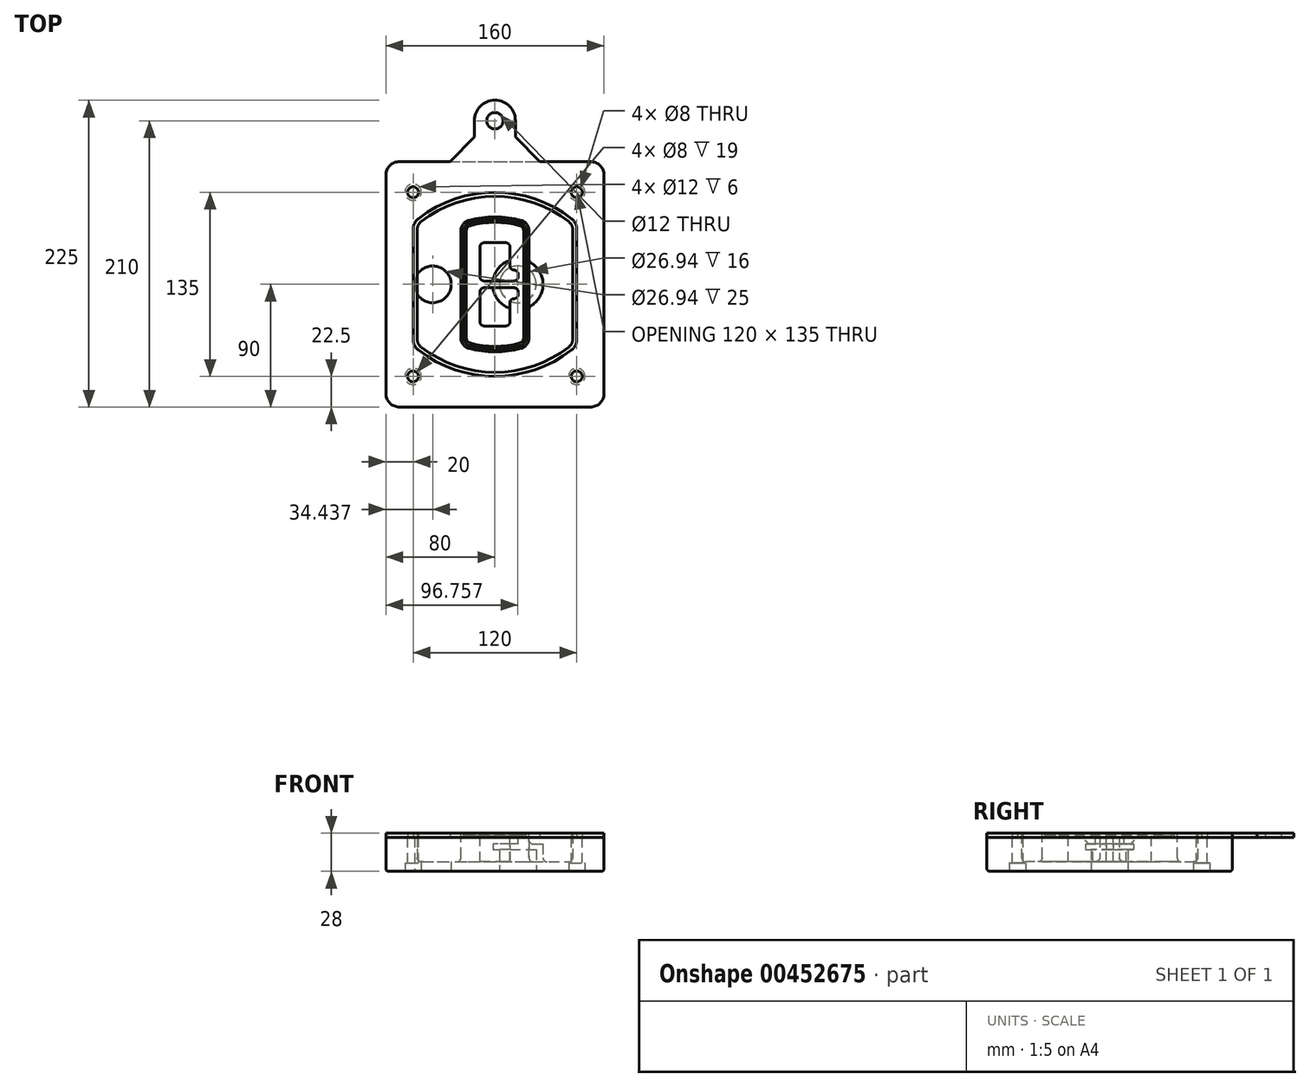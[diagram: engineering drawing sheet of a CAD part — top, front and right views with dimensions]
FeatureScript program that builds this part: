
annotation { "Feature Type Name" : "Feature", "Feature Type Description" : "" }
export const myFeature = defineFeature(function(context is Context, id is Id, definition is map)
    precondition{}
    {
        {
            var Q0;
            Q0=qCreatedBy(makeId("Top.planeOp"),FACE);
            var sketch = newSketch(context, id + "F0", { "sketchPlane" : qUnion([Q0])});
            skPoint(sketch, "E0.rect.middle", {"position": v(0, 0) * mm});
            skLineSegment(sketch, "E1.bottom", {"start": v(-70, -90) * mm, "end": v(70, -90) * mm});
            skLineSegment(sketch, "E1.top", {"start": v(-70, 90) * mm, "end": v(70, 90) * mm});
            skLineSegment(sketch, "E1.left", {"start": v(-80, -80) * mm, "end": v(-80, 80) * mm});
            skLineSegment(sketch, "E1.right", {"start": v(80, -80) * mm, "end": v(80, 80) * mm});
            skLineSegment(sketch, "E2", {"start": v(-80, 90) * mm, "end": v(80, -90) * mm, "construction": true});
            skLineSegment(sketch, "E3", {"start": v(80, 90) * mm, "end": v(-80, -90) * mm, "construction": true});
            skCircle(sketch, "E4", {"center": v(-60, 67.5) * mm, "radius": 4 * mm});
            skCircle(sketch, "E5", {"center": v(60, 67.5) * mm, "radius": 4 * mm});
            skCircle(sketch, "E6", {"center": v(60, -67.5) * mm, "radius": 4 * mm});
            skCircle(sketch, "E7", {"center": v(-60, -67.5) * mm, "radius": 4 * mm});
            skLineSegment(sketch, "E8", {"start": v(-60, 67.5) * mm, "end": v(60, 67.5) * mm, "construction": true});
            skLineSegment(sketch, "E9", {"start": v(60, 67.5) * mm, "end": v(60, -67.5) * mm, "construction": true});
            skLineSegment(sketch, "E10", {"start": v(60, -67.5) * mm, "end": v(-60, -67.5) * mm, "construction": true});
            skLineSegment(sketch, "E11", {"start": v(-60, -67.5) * mm, "end": v(-60, 67.5) * mm, "construction": true});
            skLineSegment(sketch, "E12", {"start": v(-60, 40.3) * mm, "end": v(-60, -40.3) * mm});
            skLineSegment(sketch, "E13", {"start": v(60, 40.3) * mm, "end": v(60, -40.3) * mm});
            skArc(sketch, "E14", {"start": v(56.15, 48.18) * mm, "mid": v(0, 67.5) * mm, "end": v(-56.15, 48.18) * mm});
            skArc(sketch, "E15", {"start": v(-56.15, -48.18) * mm, "mid": v(0, -67.5) * mm, "end": v(56.15, -48.18) * mm});
            skLineSegment(sketch, "E16", {"start": v(-60, 0) * mm, "end": v(60, 0) * mm, "construction": true});
            skPoint(sketch, "E17.visualSharp", {"position": v(-60, -45) * mm});
            skArc(sketch, "E17.filletArc", {"start": v(-60, -40.3) * mm, "mid": v(-58.99, -44.68) * mm, "end": v(-56.15, -48.18) * mm});
            skPoint(sketch, "E18.visualSharp", {"position": v(-60, 45) * mm});
            skArc(sketch, "E18.filletArc", {"start": v(-56.15, 48.18) * mm, "mid": v(-58.99, 44.68) * mm, "end": v(-60, 40.3) * mm});
            skPoint(sketch, "E19.visualSharp", {"position": v(60, 45) * mm});
            skArc(sketch, "E19.filletArc", {"start": v(60, 40.3) * mm, "mid": v(58.99, 44.68) * mm, "end": v(56.15, 48.18) * mm});
            skPoint(sketch, "E20.visualSharp", {"position": v(60, -45) * mm});
            skArc(sketch, "E20.filletArc", {"start": v(56.15, -48.18) * mm, "mid": v(58.99, -44.68) * mm, "end": v(60, -40.3) * mm});
            skPoint(sketch, "E21.visualSharp", {"position": v(-80, 90) * mm});
            skArc(sketch, "E21.filletArc", {"start": v(-70, 90) * mm, "mid": v(-77.07, 87.07) * mm, "end": v(-80, 80) * mm});
            skPoint(sketch, "E22.visualSharp", {"position": v(80, 90) * mm});
            skArc(sketch, "E22.filletArc", {"start": v(80, 80) * mm, "mid": v(77.07, 87.07) * mm, "end": v(70, 90) * mm});
            skPoint(sketch, "E23.visualSharp", {"position": v(80, -90) * mm});
            skArc(sketch, "E23.filletArc", {"start": v(70, -90) * mm, "mid": v(77.07, -87.07) * mm, "end": v(80, -80) * mm});
            skPoint(sketch, "E24.visualSharp", {"position": v(-80, -90) * mm});
            skArc(sketch, "E24.filletArc", {"start": v(-80, -80) * mm, "mid": v(-77.07, -87.07) * mm, "end": v(-70, -90) * mm});
            skArc(sketch, "E25.0", {"start": v(57, 40.3) * mm, "mid": v(56.3, 43.36) * mm, "end": v(54.3, 45.81) * mm});
            skLineSegment(sketch, "E25.1", {"start": v(57, 40.3) * mm, "end": v(57, -40.3) * mm});
            skArc(sketch, "E25.2", {"start": v(54.3, -45.81) * mm, "mid": v(56.3, -43.36) * mm, "end": v(57, -40.3) * mm});
            skArc(sketch, "E25.3", {"start": v(-54.3, -45.81) * mm, "mid": v(0, -64.5) * mm, "end": v(54.3, -45.81) * mm});
            skArc(sketch, "E25.4", {"start": v(-57, -40.3) * mm, "mid": v(-56.3, -43.36) * mm, "end": v(-54.3, -45.81) * mm});
            skArc(sketch, "E25.5", {"start": v(54.3, 45.81) * mm, "mid": v(0, 64.5) * mm, "end": v(-54.3, 45.81) * mm});
            skLineSegment(sketch, "E25.6", {"start": v(-57, 40.3) * mm, "end": v(-57, -40.3) * mm});
            skArc(sketch, "E25.7", {"start": v(-54.3, 45.81) * mm, "mid": v(-56.3, 43.36) * mm, "end": v(-57, 40.3) * mm});
            skArc(sketch, "E26.0", {"start": v(-58.62, 51.33) * mm, "mid": v(-62.58, 46.43) * mm, "end": v(-64, 40.3) * mm});
            skArc(sketch, "E26.1", {"start": v(58.62, 51.33) * mm, "mid": v(0, 71.5) * mm, "end": v(-58.62, 51.33) * mm});
            skArc(sketch, "E26.2", {"start": v(64, 40.3) * mm, "mid": v(62.58, 46.43) * mm, "end": v(58.62, 51.33) * mm});
            skLineSegment(sketch, "E26.3", {"start": v(64, 40.3) * mm, "end": v(64, -40.3) * mm});
            skArc(sketch, "E26.4", {"start": v(58.62, -51.33) * mm, "mid": v(62.58, -46.43) * mm, "end": v(64, -40.3) * mm});
            skLineSegment(sketch, "E26.5", {"start": v(-64, 40.3) * mm, "end": v(-64, -40.3) * mm});
            skArc(sketch, "E26.6", {"start": v(-58.62, -51.33) * mm, "mid": v(0, -71.5) * mm, "end": v(58.62, -51.33) * mm});
            skArc(sketch, "E26.7", {"start": v(-64, -40.3) * mm, "mid": v(-62.58, -46.43) * mm, "end": v(-58.62, -51.33) * mm});
            skSolve(sketch);
        }
        {
            var Q0;
            Q0=makeQuery(id+"F0.imprint","IMPRINT",FACE,{"disambiguationData":[TD([[makeQuery(id+"F0.imprint","IMPRINT",EDGE,{"derivedFrom":sQuery(id+"F0.wireOp",EDGE,"E1.bottom")}),1.0]])]});
            var Q1;
            Q1=makeQuery(id+"F0.imprint","IMPRINT",FACE,{"disambiguationData":[TD([[makeQuery(id+"F0.imprint","IMPRINT",EDGE,{"derivedFrom":sQuery(id+"F0.wireOp",EDGE,"E12")}),1.0]])]});
            var Q2;
            Q2=makeQuery(id+"F0.imprint","IMPRINT",FACE,{"disambiguationData":[TD([[makeQuery(id+"F0.imprint","IMPRINT",EDGE,{"derivedFrom":sQuery(id+"F0.wireOp",EDGE,"E25.0")}),1.0]])]});
            var Q3;
            Q3=makeQuery(id+"F0.imprint","IMPRINT",FACE,{"disambiguationData":[TD([[makeQuery(id+"F0.imprint","IMPRINT",EDGE,{"derivedFrom":sQuery(id+"F0.wireOp",EDGE,"E12")}),-1.0]])]});
            extrude(context, id + "F1", {"entities" : qUnion([Q0, Q1, Q2, Q3]), "oppositeDirection" : true, "depth" : 25 * mm});
        }
        {
            var Q0;
            Q0=makeQuery(id+"F0.imprint","IMPRINT",FACE,{"disambiguationData":[TD([[makeQuery(id+"F0.imprint","IMPRINT",EDGE,{"derivedFrom":sQuery(id+"F0.wireOp",EDGE,"E12")}),1.0]])]});
            extrude(context, id + "F2", {"entities" : qUnion([Q0]), "operationType" : NewBodyOperationType.ADD, "depth" : 3 * mm});
        }
        {
            var Q0;
            Q0=makeQuery(id+"F0.imprint","IMPRINT",FACE,{"disambiguationData":[TD([[makeQuery(id+"F0.imprint","IMPRINT",EDGE,{"derivedFrom":sQuery(id+"F0.wireOp",EDGE,"E25.0")}),1.0]])]});
            extrude(context, id + "F3", {"entities" : qUnion([Q0]), "operationType" : NewBodyOperationType.REMOVE, "oppositeDirection" : true, "depth" : 18 * mm});
        }
        {
            var Q0;
            Q0=makeQuery(id+"F2.opExtrude","CAP_FACE",FACE,{"disambiguationData":[OSD([sQuery(id+"F0.wireOp",EDGE,"E12"),sQuery(id+"F0.wireOp",EDGE,"E13"),sQuery(id+"F0.wireOp",EDGE,"E14"),sQuery(id+"F0.wireOp",EDGE,"E15"),sQuery(id+"F0.wireOp",EDGE,"E17.filletArc"),sQuery(id+"F0.wireOp",EDGE,"E18.filletArc"),sQuery(id+"F0.wireOp",EDGE,"E19.filletArc"),sQuery(id+"F0.wireOp",EDGE,"E20.filletArc"),sQuery(id+"F0.wireOp",EDGE,"E25.0"),sQuery(id+"F0.wireOp",EDGE,"E25.1"),sQuery(id+"F0.wireOp",EDGE,"E25.2"),sQuery(id+"F0.wireOp",EDGE,"E25.3"),sQuery(id+"F0.wireOp",EDGE,"E25.4"),sQuery(id+"F0.wireOp",EDGE,"E25.5"),sQuery(id+"F0.wireOp",EDGE,"E25.6"),sQuery(id+"F0.wireOp",EDGE,"E25.7")])],"isStart":false});
            var sketch = newSketch(context, id + "F4", { "sketchPlane" : qUnion([Q0])});
            skArc(sketch, "E27.0", {"start": v(-19.08, -46.97) * mm, "mid": v(0, -49.5) * mm, "end": v(19.08, -46.97) * mm});
            skArc(sketch, "E28.0", {"start": v(19.08, 46.97) * mm, "mid": v(0, 49.5) * mm, "end": v(-19.08, 46.97) * mm});
            skLineSegment(sketch, "E29", {"start": v(-25, 39.25) * mm, "end": v(-25, -39.25) * mm});
            skLineSegment(sketch, "E30", {"start": v(25, 39.25) * mm, "end": v(25, -39.25) * mm});
            skLineSegment(sketch, "E31", {"start": v(-25, 45.1) * mm, "end": v(25, 45.1) * mm, "construction": true});
            skLineSegment(sketch, "E32", {"start": v(-25, -45.1) * mm, "end": v(25, -45.1) * mm, "construction": true});
            skPoint(sketch, "E33.visualSharp", {"position": v(-25, 45.1) * mm});
            skArc(sketch, "E33.filletArc", {"start": v(-19.08, 46.97) * mm, "mid": v(-23.35, 44.11) * mm, "end": v(-25, 39.25) * mm});
            skPoint(sketch, "E34.visualSharp", {"position": v(25, 45.1) * mm});
            skArc(sketch, "E34.filletArc", {"start": v(25, 39.25) * mm, "mid": v(23.35, 44.11) * mm, "end": v(19.08, 46.97) * mm});
            skPoint(sketch, "E35.visualSharp", {"position": v(25, -45.1) * mm});
            skArc(sketch, "E35.filletArc", {"start": v(19.08, -46.97) * mm, "mid": v(23.35, -44.11) * mm, "end": v(25, -39.25) * mm});
            skPoint(sketch, "E36.visualSharp", {"position": v(-25, -45.1) * mm});
            skArc(sketch, "E36.filletArc", {"start": v(-25, -39.25) * mm, "mid": v(-23.35, -44.11) * mm, "end": v(-19.08, -46.97) * mm});
            skArc(sketch, "E37.0", {"start": v(54.3, 45.81) * mm, "mid": v(0, 64.5) * mm, "end": v(-54.3, 45.81) * mm});
            skArc(sketch, "E37.1", {"start": v(-54.3, 45.81) * mm, "mid": v(-56.3, 43.36) * mm, "end": v(-57, 40.3) * mm});
            skLineSegment(sketch, "E37.2", {"start": v(-57, 40.3) * mm, "end": v(-57, -40.3) * mm});
            skArc(sketch, "E37.3", {"start": v(-57, -40.3) * mm, "mid": v(-56.3, -43.36) * mm, "end": v(-54.3, -45.81) * mm});
            skArc(sketch, "E37.4", {"start": v(-54.3, -45.81) * mm, "mid": v(0, -64.5) * mm, "end": v(54.3, -45.81) * mm});
            skArc(sketch, "E37.5", {"start": v(54.3, -45.81) * mm, "mid": v(56.3, -43.36) * mm, "end": v(57, -40.3) * mm});
            skLineSegment(sketch, "E37.6", {"start": v(57, 40.3) * mm, "end": v(57, -40.3) * mm});
            skArc(sketch, "E37.7", {"start": v(57, 40.3) * mm, "mid": v(56.3, 43.36) * mm, "end": v(54.3, 45.81) * mm});
            skLineSegment(sketch, "E38.0", {"start": v(23, 39.25) * mm, "end": v(23, -39.25) * mm});
            skArc(sketch, "E38.1", {"start": v(18.56, -45.04) * mm, "mid": v(21.76, -42.9) * mm, "end": v(23, -39.25) * mm});
            skArc(sketch, "E38.2", {"start": v(-18.56, -45.04) * mm, "mid": v(0, -47.5) * mm, "end": v(18.56, -45.04) * mm});
            skArc(sketch, "E38.3", {"start": v(-23, -39.25) * mm, "mid": v(-21.76, -42.9) * mm, "end": v(-18.56, -45.04) * mm});
            skLineSegment(sketch, "E38.4", {"start": v(-23, 39.25) * mm, "end": v(-23, -39.25) * mm});
            skArc(sketch, "E38.5", {"start": v(23, 39.25) * mm, "mid": v(21.76, 42.9) * mm, "end": v(18.56, 45.04) * mm});
            skArc(sketch, "E38.6", {"start": v(-18.56, 45.04) * mm, "mid": v(-21.76, 42.9) * mm, "end": v(-23, 39.25) * mm});
            skArc(sketch, "E38.7", {"start": v(18.56, 45.04) * mm, "mid": v(0, 47.5) * mm, "end": v(-18.56, 45.04) * mm});
            skArc(sketch, "E39.0", {"start": v(21, 39.25) * mm, "mid": v(20.18, 41.68) * mm, "end": v(18.04, 43.1) * mm});
            skLineSegment(sketch, "E39.1", {"start": v(21, 39.25) * mm, "end": v(21, -39.25) * mm});
            skArc(sketch, "E39.2", {"start": v(18.04, -43.1) * mm, "mid": v(20.18, -41.68) * mm, "end": v(21, -39.25) * mm});
            skArc(sketch, "E39.3", {"start": v(-18.04, -43.1) * mm, "mid": v(0, -45.5) * mm, "end": v(18.04, -43.1) * mm});
            skArc(sketch, "E39.4", {"start": v(-21, -39.25) * mm, "mid": v(-20.18, -41.68) * mm, "end": v(-18.04, -43.1) * mm});
            skArc(sketch, "E39.5", {"start": v(18.04, 43.1) * mm, "mid": v(0, 45.5) * mm, "end": v(-18.04, 43.1) * mm});
            skLineSegment(sketch, "E39.6", {"start": v(-21, 39.25) * mm, "end": v(-21, -39.25) * mm});
            skArc(sketch, "E39.7", {"start": v(-18.04, 43.1) * mm, "mid": v(-20.18, 41.68) * mm, "end": v(-21, 39.25) * mm});
            skLineSegment(sketch, "E40", {"start": v(-25, 0) * mm, "end": v(25, 0) * mm, "construction": true});
            skLineSegment(sketch, "E41", {"start": v(-11, 5.5) * mm, "end": v(-11, 27.5) * mm});
            skLineSegment(sketch, "E42", {"start": v(-8, 30.5) * mm, "end": v(8, 30.5) * mm});
            skLineSegment(sketch, "E43", {"start": v(11, 27.5) * mm, "end": v(11, 13.5) * mm});
            skLineSegment(sketch, "E44", {"start": v(14, 10.5) * mm, "end": v(14, 10.5) * mm});
            skLineSegment(sketch, "E45", {"start": v(17, 7.5) * mm, "end": v(17, 5.5) * mm});
            skLineSegment(sketch, "E46", {"start": v(14, 2.5) * mm, "end": v(-8, 2.5) * mm});
            skPoint(sketch, "E47.visualSharp", {"position": v(-11, 30.5) * mm});
            skArc(sketch, "E47.filletArc", {"start": v(-8, 30.5) * mm, "mid": v(-10.12, 29.62) * mm, "end": v(-11, 27.5) * mm});
            skPoint(sketch, "E48.visualSharp", {"position": v(11, 30.5) * mm});
            skArc(sketch, "E48.filletArc", {"start": v(11, 27.5) * mm, "mid": v(10.12, 29.62) * mm, "end": v(8, 30.5) * mm});
            skPoint(sketch, "E49.visualSharp", {"position": v(11, 10.5) * mm});
            skArc(sketch, "E49.filletArc", {"start": v(11, 13.5) * mm, "mid": v(11.88, 11.38) * mm, "end": v(14, 10.5) * mm});
            skPoint(sketch, "E50.visualSharp", {"position": v(17, 10.5) * mm});
            skArc(sketch, "E50.filletArc", {"start": v(17, 7.5) * mm, "mid": v(16.12, 9.62) * mm, "end": v(14, 10.5) * mm});
            skPoint(sketch, "E51.visualSharp", {"position": v(17, 2.5) * mm});
            skArc(sketch, "E51.filletArc", {"start": v(14, 2.5) * mm, "mid": v(16.12, 3.38) * mm, "end": v(17, 5.5) * mm});
            skPoint(sketch, "E52.visualSharp", {"position": v(-11, 2.5) * mm});
            skArc(sketch, "E52.filletArc", {"start": v(-11, 5.5) * mm, "mid": v(-10.12, 3.38) * mm, "end": v(-8, 2.5) * mm});
            skLineSegment(sketch, "E53.0.MirrorCS", {"start": v(14, -2.5) * mm, "end": v(-8, -2.5) * mm});
            skArc(sketch, "E54.0.MirrorCS", {"start": v(-11, -5.5) * mm, "mid": v(-10.12, -3.38) * mm, "end": v(-8, -2.5) * mm});
            skLineSegment(sketch, "E55.0.MirrorCS", {"start": v(-11, -5.5) * mm, "end": v(-11, -27.5) * mm});
            skArc(sketch, "E56.0.MirrorCS", {"start": v(-8, -30.5) * mm, "mid": v(-10.12, -29.62) * mm, "end": v(-11, -27.5) * mm});
            skLineSegment(sketch, "E57.0.MirrorCS", {"start": v(-8, -30.5) * mm, "end": v(8, -30.5) * mm});
            skArc(sketch, "E58.0.MirrorCS", {"start": v(11, -27.5) * mm, "mid": v(10.12, -29.62) * mm, "end": v(8, -30.5) * mm});
            skLineSegment(sketch, "E59.0.MirrorCS", {"start": v(11, -27.5) * mm, "end": v(11, -13.5) * mm});
            skArc(sketch, "E60.0.MirrorCS", {"start": v(11, -13.5) * mm, "mid": v(11.88, -11.38) * mm, "end": v(14, -10.5) * mm});
            skArc(sketch, "E61.0.MirrorCS", {"start": v(17, -7.5) * mm, "mid": v(16.12, -9.62) * mm, "end": v(14, -10.5) * mm});
            skLineSegment(sketch, "E62.0.MirrorCS", {"start": v(17, -7.5) * mm, "end": v(17, -5.5) * mm});
            skArc(sketch, "E63.0.MirrorCS", {"start": v(14, -2.5) * mm, "mid": v(16.12, -3.38) * mm, "end": v(17, -5.5) * mm});
            skSolve(sketch);
        }
        {
            var Q0;
            Q0=makeQuery(id+"F4.imprint","IMPRINT",FACE,{"disambiguationData":[TD([[makeQuery(id+"F4.imprint","IMPRINT",EDGE,{"derivedFrom":sQuery(id+"F4.wireOp",EDGE,"E27.0")}),1.0]])]});
            var Q1;
            Q1=makeQuery(id+"F4.imprint","IMPRINT",FACE,{"disambiguationData":[TD([[makeQuery(id+"F4.imprint","IMPRINT",EDGE,{"derivedFrom":sQuery(id+"F4.wireOp",EDGE,"E38.0")}),-1.0]])]});
            var Q2;
            Q2=makeQuery(id+"F4.imprint","IMPRINT",FACE,{"disambiguationData":[TD([[makeQuery(id+"F4.imprint","IMPRINT",EDGE,{"derivedFrom":sQuery(id+"F4.wireOp",EDGE,"E39.0")}),1.0]])]});
            extrude(context, id + "F5", {"entities" : qUnion([Q0, Q1, Q2]), "operationType" : NewBodyOperationType.ADD, "endBound" : BoundingType.UP_TO_NEXT, "oppositeDirection" : true, "depth" : 25 * mm});
        }
        {
            var Q0;
            Q0=makeQuery(id+"F4.imprint","IMPRINT",FACE,{"disambiguationData":[TD([[makeQuery(id+"F4.imprint","IMPRINT",EDGE,{"derivedFrom":sQuery(id+"F4.wireOp",EDGE,"E38.0")}),-1.0]])]});
            extrude(context, id + "F6", {"entities" : qUnion([Q0]), "operationType" : NewBodyOperationType.REMOVE, "oppositeDirection" : true, "depth" : 2 * mm});
        }
        {
            var Q0;
            Q0=makeQuery(id+"F1.opExtrude","CAP_FACE",FACE,{"disambiguationData":[OSD([sQuery(id+"F0.wireOp",EDGE,"E1.bottom"),sQuery(id+"F0.wireOp",EDGE,"E1.top"),sQuery(id+"F0.wireOp",EDGE,"E1.left"),sQuery(id+"F0.wireOp",EDGE,"E1.right"),sQuery(id+"F0.wireOp",EDGE,"E4"),sQuery(id+"F0.wireOp",EDGE,"E5"),sQuery(id+"F0.wireOp",EDGE,"E6"),sQuery(id+"F0.wireOp",EDGE,"E7"),sQuery(id+"F0.wireOp",EDGE,"E21.filletArc"),sQuery(id+"F0.wireOp",EDGE,"E22.filletArc"),sQuery(id+"F0.wireOp",EDGE,"E23.filletArc"),sQuery(id+"F0.wireOp",EDGE,"E24.filletArc")])],"isStart":false});
            var sketch = newSketch(context, id + "F7", { "sketchPlane" : qUnion([Q0])});
            skCircle(sketch, "E64", {"center": v(16.76, 0) * mm, "radius": 13.47 * mm});
            skCircle(sketch, "E65", {"center": v(-45.56, 0) * mm, "radius": 13.47 * mm});
            skLineSegment(sketch, "E66", {"start": v(80, 0) * mm, "end": v(-80, 0) * mm});
            skCircle(sketch, "E67", {"center": v(16.76, 0) * mm, "radius": 18.47 * mm});
            skCircle(sketch, "E68", {"center": v(60, -67.5) * mm, "radius": 6 * mm});
            skCircle(sketch, "E69", {"center": v(-60, -67.5) * mm, "radius": 6 * mm});
            skCircle(sketch, "E70", {"center": v(-60, 67.5) * mm, "radius": 6 * mm});
            skCircle(sketch, "E71", {"center": v(60, 67.5) * mm, "radius": 6 * mm});
            skSolve(sketch);
        }
        {
            var Q0;
            {var subQ1=sQuery(id+"F7.wireOp",EDGE,"E66");var subQ4=sQuery(id+"F7.wireOp",EDGE,"E64");var subQ6=makeQuery(id+"F7.imprint","INTERSECT",VERTEX,{"disambiguationData":[OD(0.0)],"derivedFrom":[subQ4,subQ1]});Q0=makeQuery(id+"F7.imprint","IMPRINT",FACE,{"disambiguationData":[TD([[makeQuery(id+"F7.imprint","IMPRINT",EDGE,{"disambiguationData":[TD([[subQ6,-1.0]])],"derivedFrom":subQ4}),-1.0]])]});}
            var Q1;
            {var subQ0=sQuery(id+"F7.wireOp",EDGE,"E66");var subQ1=sQuery(id+"F7.wireOp",EDGE,"E64");var subQ3=makeQuery(id+"F7.imprint","INTERSECT",VERTEX,{"disambiguationData":[OD(0.0)],"derivedFrom":[subQ1,subQ0]});Q1=makeQuery(id+"F7.imprint","IMPRINT",FACE,{"disambiguationData":[TD([[makeQuery(id+"F7.imprint","IMPRINT",EDGE,{"disambiguationData":[TD([[subQ3,-1.0]])],"derivedFrom":subQ1}),1.0]])]});}
            var Q2;
            {var subQ0=sQuery(id+"F7.wireOp",EDGE,"E66");var subQ1=sQuery(id+"F7.wireOp",EDGE,"E64");var subQ3=makeQuery(id+"F7.imprint","INTERSECT",VERTEX,{"disambiguationData":[OD(0.0)],"derivedFrom":[subQ1,subQ0]});Q2=makeQuery(id+"F7.imprint","IMPRINT",FACE,{"disambiguationData":[TD([[makeQuery(id+"F7.imprint","IMPRINT",EDGE,{"disambiguationData":[TD([[subQ3,1.0]])],"derivedFrom":subQ1}),1.0]])]});}
            var Q3;
            {var subQ1=sQuery(id+"F7.wireOp",EDGE,"E66");var subQ4=sQuery(id+"F7.wireOp",EDGE,"E64");var subQ6=makeQuery(id+"F7.imprint","INTERSECT",VERTEX,{"disambiguationData":[OD(0.0)],"derivedFrom":[subQ4,subQ1]});Q3=makeQuery(id+"F7.imprint","IMPRINT",FACE,{"disambiguationData":[TD([[makeQuery(id+"F7.imprint","IMPRINT",EDGE,{"disambiguationData":[TD([[subQ6,1.0]])],"derivedFrom":subQ4}),-1.0]])]});}
            extrude(context, id + "F8", {"entities" : qUnion([Q0, Q1, Q2, Q3]), "operationType" : NewBodyOperationType.ADD, "oppositeDirection" : true, "depth" : 20 * mm});
        }
        {
            var Q0;
            {var subQ0=sQuery(id+"F7.wireOp",EDGE,"E66");var subQ1=sQuery(id+"F7.wireOp",EDGE,"E64");var subQ3=makeQuery(id+"F7.imprint","INTERSECT",VERTEX,{"disambiguationData":[OD(0.0)],"derivedFrom":[subQ1,subQ0]});Q0=makeQuery(id+"F7.imprint","IMPRINT",FACE,{"disambiguationData":[TD([[makeQuery(id+"F7.imprint","IMPRINT",EDGE,{"disambiguationData":[TD([[subQ3,-1.0]])],"derivedFrom":subQ1}),1.0]])]});}
            var Q1;
            {var subQ0=sQuery(id+"F7.wireOp",EDGE,"E66");var subQ1=sQuery(id+"F7.wireOp",EDGE,"E64");var subQ3=makeQuery(id+"F7.imprint","INTERSECT",VERTEX,{"disambiguationData":[OD(0.0)],"derivedFrom":[subQ1,subQ0]});Q1=makeQuery(id+"F7.imprint","IMPRINT",FACE,{"disambiguationData":[TD([[makeQuery(id+"F7.imprint","IMPRINT",EDGE,{"disambiguationData":[TD([[subQ3,1.0]])],"derivedFrom":subQ1}),1.0]])]});}
            extrude(context, id + "F9", {"entities" : qUnion([Q0, Q1]), "operationType" : NewBodyOperationType.REMOVE, "oppositeDirection" : true, "depth" : 16 * mm});
        }
        {
            var Q0;
            {var subQ0=sQuery(id+"F7.wireOp",EDGE,"E66");var subQ1=sQuery(id+"F7.wireOp",EDGE,"E65");var subQ3=makeQuery(id+"F7.imprint","INTERSECT",VERTEX,{"disambiguationData":[OD(0.0)],"derivedFrom":[subQ1,subQ0]});Q0=makeQuery(id+"F7.imprint","IMPRINT",FACE,{"disambiguationData":[TD([[makeQuery(id+"F7.imprint","IMPRINT",EDGE,{"disambiguationData":[TD([[subQ3,-1.0]])],"derivedFrom":subQ1}),1.0]])]});}
            var Q1;
            {var subQ0=sQuery(id+"F7.wireOp",EDGE,"E66");var subQ1=sQuery(id+"F7.wireOp",EDGE,"E65");var subQ3=makeQuery(id+"F7.imprint","INTERSECT",VERTEX,{"disambiguationData":[OD(0.0)],"derivedFrom":[subQ1,subQ0]});Q1=makeQuery(id+"F7.imprint","IMPRINT",FACE,{"disambiguationData":[TD([[makeQuery(id+"F7.imprint","IMPRINT",EDGE,{"disambiguationData":[TD([[subQ3,1.0]])],"derivedFrom":subQ1}),1.0]])]});}
            extrude(context, id + "F10", {"entities" : qUnion([Q0, Q1]), "operationType" : NewBodyOperationType.REMOVE, "oppositeDirection" : true, "depth" : 25 * mm});
        }
        {
            var Q0;
            Q0=makeQuery(id+"F7.imprint","IMPRINT",FACE,{"disambiguationData":[TD([[makeQuery(id+"F7.imprint","IMPRINT",EDGE,{"derivedFrom":sQuery(id+"F7.wireOp",EDGE,"E68")}),1.0]])]});
            var Q1;
            Q1=makeQuery(id+"F7.imprint","IMPRINT",FACE,{"disambiguationData":[TD([[makeQuery(id+"F7.imprint","IMPRINT",EDGE,{"derivedFrom":makeQuery(id+"F1.opExtrude","CAP_EDGE",EDGE,{"disambiguationData":[OSD([sQuery(id+"F0.wireOp",EDGE,"E5")])],"isStart":false})}),-1.0]])]});
            var Q2;
            Q2=makeQuery(id+"F7.imprint","IMPRINT",FACE,{"disambiguationData":[TD([[makeQuery(id+"F7.imprint","IMPRINT",EDGE,{"derivedFrom":sQuery(id+"F7.wireOp",EDGE,"E69")}),1.0]])]});
            var Q3;
            Q3=makeQuery(id+"F7.imprint","IMPRINT",FACE,{"disambiguationData":[TD([[makeQuery(id+"F7.imprint","IMPRINT",EDGE,{"derivedFrom":makeQuery(id+"F1.opExtrude","CAP_EDGE",EDGE,{"disambiguationData":[OSD([sQuery(id+"F0.wireOp",EDGE,"E4")])],"isStart":false})}),-1.0]])]});
            var Q4;
            Q4=makeQuery(id+"F7.imprint","IMPRINT",FACE,{"disambiguationData":[TD([[makeQuery(id+"F7.imprint","IMPRINT",EDGE,{"derivedFrom":sQuery(id+"F7.wireOp",EDGE,"E70")}),1.0]])]});
            var Q5;
            Q5=makeQuery(id+"F7.imprint","IMPRINT",FACE,{"disambiguationData":[TD([[makeQuery(id+"F7.imprint","IMPRINT",EDGE,{"derivedFrom":makeQuery(id+"F1.opExtrude","CAP_EDGE",EDGE,{"disambiguationData":[OSD([sQuery(id+"F0.wireOp",EDGE,"E7")])],"isStart":false})}),-1.0]])]});
            var Q6;
            Q6=makeQuery(id+"F7.imprint","IMPRINT",FACE,{"disambiguationData":[TD([[makeQuery(id+"F7.imprint","IMPRINT",EDGE,{"derivedFrom":sQuery(id+"F7.wireOp",EDGE,"E71")}),1.0]])]});
            var Q7;
            Q7=makeQuery(id+"F7.imprint","IMPRINT",FACE,{"disambiguationData":[TD([[makeQuery(id+"F7.imprint","IMPRINT",EDGE,{"derivedFrom":makeQuery(id+"F1.opExtrude","CAP_EDGE",EDGE,{"disambiguationData":[OSD([sQuery(id+"F0.wireOp",EDGE,"E6")])],"isStart":false})}),-1.0]])]});
            extrude(context, id + "F11", {"entities" : qUnion([Q0, Q1, Q2, Q3, Q4, Q5, Q6, Q7]), "operationType" : NewBodyOperationType.REMOVE, "oppositeDirection" : true, "depth" : 6 * mm});
        }
        {
            var Q0;
            Q0=makeQuery(id+"F9.boolean.opBoolean","COPY",FACE,{"derivedFrom":makeQuery(id+"F9.opExtrude","CAP_FACE",FACE,{"disambiguationData":[OSD([sQuery(id+"F7.wireOp",EDGE,"E64")])],"isStart":false})});
            var sketch = newSketch(context, id + "F12", { "sketchPlane" : qUnion([Q0])});
            skArc(sketch, "E72.0", {"start": v(11, 17.55) * mm, "mid": v(2.57, 11.82) * mm, "end": v(-1.54, 2.5) * mm});
            skArc(sketch, "E72.1", {"start": v(-1.54, -2.5) * mm, "mid": v(2.57, -11.82) * mm, "end": v(11, -17.55) * mm});
            skLineSegment(sketch, "E73", {"start": v(-1.54, -2.5) * mm, "end": v(14, -2.5) * mm});
            skLineSegment(sketch, "E74.0", {"start": v(14, 2.5) * mm, "end": v(-1.54, 2.5) * mm});
            skArc(sketch, "E74.1", {"start": v(14, 2.5) * mm, "mid": v(16.12, 3.38) * mm, "end": v(17, 5.5) * mm});
            skLineSegment(sketch, "E74.2", {"start": v(17, 7.5) * mm, "end": v(17, 5.5) * mm});
            skArc(sketch, "E74.3", {"start": v(17, 7.5) * mm, "mid": v(16.12, 9.62) * mm, "end": v(14, 10.5) * mm});
            skArc(sketch, "E74.4", {"start": v(11, 13.5) * mm, "mid": v(11.88, 11.38) * mm, "end": v(14, 10.5) * mm});
            skLineSegment(sketch, "E74.5", {"start": v(11, 17.55) * mm, "end": v(11, 13.5) * mm});
            skLineSegment(sketch, "E74.7", {"start": v(14, -2.5) * mm, "end": v(-1.54, -2.5) * mm});
            skArc(sketch, "E74.8", {"start": v(14, -2.5) * mm, "mid": v(16.12, -3.38) * mm, "end": v(17, -5.5) * mm});
            skLineSegment(sketch, "E74.9", {"start": v(17, -7.5) * mm, "end": v(17, -5.5) * mm});
            skArc(sketch, "E74.10", {"start": v(17, -7.5) * mm, "mid": v(16.12, -9.62) * mm, "end": v(14, -10.5) * mm});
            skArc(sketch, "E74.11", {"start": v(11, -13.5) * mm, "mid": v(11.88, -11.38) * mm, "end": v(14, -10.5) * mm});
            skLineSegment(sketch, "E74.12", {"start": v(11, -17.55) * mm, "end": v(11, -13.5) * mm});
            skPoint(sketch, "E75.orphan", {"position": v(11, -27.5) * mm});
            skPoint(sketch, "E76.orphan", {"position": v(-8, -2.5) * mm});
            skPoint(sketch, "E77.orphan", {"position": v(-8, 2.5) * mm});
            skPoint(sketch, "E78.orphan", {"position": v(11, 27.5) * mm});
            skSolve(sketch);
        }
        {
            var Q0;
            {var subQ7=sQuery(id+"F12.wireOp",EDGE,"E72.0");var subQ14=sQuery(id+"F12.wireOp",EDGE,"E72.1");var subQ16=sQuery(id+"F12.wireOp",EDGE,"E74.1");var subQ18=sQuery(id+"F12.wireOp",EDGE,"E74.8");Q0=qUnion([makeQuery(id+"F12.imprint","IMPRINT",FACE,{"disambiguationData":[TD([[makeQuery(id+"F12.imprint","IMPRINT",EDGE,{"derivedFrom":subQ7}),1.0]])]}),makeQuery(id+"F12.imprint","IMPRINT",FACE,{"disambiguationData":[TD([[makeQuery(id+"F12.imprint","IMPRINT",EDGE,{"derivedFrom":subQ14}),1.0]])]}),makeQuery(id+"F12.imprint","IMPRINT",FACE,{"disambiguationData":[TD([[makeQuery(id+"F12.imprint","IMPRINT",EDGE,{"derivedFrom":subQ16}),1.0]])]}),makeQuery(id+"F12.imprint","IMPRINT",FACE,{"disambiguationData":[TD([[makeQuery(id+"F12.imprint","IMPRINT",EDGE,{"derivedFrom":subQ18}),-1.0]])]})]);}
            var Q1;
            Q1=makeQuery(id+"F5.boolean.opBoolean","SPLIT",FACE,{"disambiguationData":[TD([makeQuery(id+"F5.opExtrude","SWEPT_FACE",FACE,{"disambiguationData":[OSD([sQuery(id+"F4.wireOp",EDGE,"E41")])]})])],"derivedFrom":makeQuery(id+"F3.boolean.opBoolean","COPY",FACE,{"derivedFrom":makeQuery(id+"F3.opExtrude","CAP_FACE",FACE,{"disambiguationData":[OSD([sQuery(id+"F0.wireOp",EDGE,"E25.0"),sQuery(id+"F0.wireOp",EDGE,"E25.1"),sQuery(id+"F0.wireOp",EDGE,"E25.2"),sQuery(id+"F0.wireOp",EDGE,"E25.3"),sQuery(id+"F0.wireOp",EDGE,"E25.4"),sQuery(id+"F0.wireOp",EDGE,"E25.5"),sQuery(id+"F0.wireOp",EDGE,"E25.6"),sQuery(id+"F0.wireOp",EDGE,"E25.7")])],"isStart":false})})});
            extrude(context, id + "F13", {"entities" : qUnion([Q0]), "operationType" : NewBodyOperationType.REMOVE, "endBound" : BoundingType.UP_TO_SURFACE, "endBoundEntityFace" : qUnion([Q1]), "depth" : 25 * mm});
        }
        {
            var Q0;
            Q0=makeQuery(id+"F3.boolean.opBoolean","COPY",EDGE,{"derivedFrom":makeQuery(id+"F3.opExtrude","CAP_EDGE",EDGE,{"disambiguationData":[OSD([sQuery(id+"F0.wireOp",EDGE,"E25.6")])],"isStart":false})});
            var Q1;
            Q1=makeQuery(id+"F8.boolean.opBoolean","INTERSECT",EDGE,{"derivedFrom":[makeQuery(id+"F5.opExtrude","SWEPT_FACE",FACE,{"disambiguationData":[OSD([sQuery(id+"F4.wireOp",EDGE,"E30")])]}),makeQuery(id+"F8.opExtrude","CAP_FACE",FACE,{"disambiguationData":[OSD([sQuery(id+"F7.wireOp",EDGE,"E67")])],"isStart":false})]});
            var Q2;
            Q2=makeQuery(id+"F8.boolean.opBoolean","INTERSECT",EDGE,{"disambiguationData":[OD(1.0)],"derivedFrom":[makeQuery(id+"F5.opExtrude","SWEPT_FACE",FACE,{"disambiguationData":[OSD([sQuery(id+"F4.wireOp",EDGE,"E30")])]}),makeQuery(id+"F8.opExtrude","SWEPT_FACE",FACE,{"disambiguationData":[OSD([sQuery(id+"F7.wireOp",EDGE,"E67")])]})]});
            var Q3;
            {var subQ0=sQuery(id+"F4.wireOp",EDGE,"E30");Q3=makeQuery(id+"F8.boolean.opBoolean","SPLIT",EDGE,{"disambiguationData":[TD([makeQuery(id+"F5.opExtrude","SWEPT_FACE",FACE,{"disambiguationData":[OSD([sQuery(id+"F4.wireOp",EDGE,"E35.filletArc")])]})])],"derivedFrom":makeQuery(id+"F5.opExtrude","CAP_EDGE",EDGE,{"disambiguationData":[OSD([subQ0])],"isStart":false})});}
            var Q4;
            {var subQ0=sQuery(id+"F0.wireOp",EDGE,"E25.7");var subQ1=sQuery(id+"F0.wireOp",EDGE,"E25.1");var subQ2=sQuery(id+"F0.wireOp",EDGE,"E25.6");var subQ3=sQuery(id+"F0.wireOp",EDGE,"E25.5");var subQ4=sQuery(id+"F0.wireOp",EDGE,"E25.4");var subQ5=sQuery(id+"F0.wireOp",EDGE,"E25.0");var subQ6=sQuery(id+"F0.wireOp",EDGE,"E25.2");var subQ7=sQuery(id+"F0.wireOp",EDGE,"E25.3");Q4=makeQuery(id+"F8.boolean.opBoolean","INTERSECT",EDGE,{"derivedFrom":[makeQuery(id+"F5.boolean.opBoolean","SPLIT",FACE,{"disambiguationData":[TD([makeQuery(id+"F2.opExtrude","SWEPT_FACE",FACE,{"disambiguationData":[OSD([subQ5])]})])],"derivedFrom":makeQuery(id+"F3.boolean.opBoolean","COPY",FACE,{"derivedFrom":makeQuery(id+"F3.opExtrude","CAP_FACE",FACE,{"disambiguationData":[OSD([subQ5,subQ1,subQ6,subQ7,subQ4,subQ3,subQ2,subQ0])],"isStart":false})})}),makeQuery(id+"F8.opExtrude","SWEPT_FACE",FACE,{"disambiguationData":[OSD([sQuery(id+"F7.wireOp",EDGE,"E67")])]})]});}
            var Q5;
            Q5=makeQuery(id+"F8.boolean.opBoolean","INTERSECT",EDGE,{"disambiguationData":[OD(0.0)],"derivedFrom":[makeQuery(id+"F5.opExtrude","SWEPT_FACE",FACE,{"disambiguationData":[OSD([sQuery(id+"F4.wireOp",EDGE,"E30")])]}),makeQuery(id+"F8.opExtrude","SWEPT_FACE",FACE,{"disambiguationData":[OSD([sQuery(id+"F7.wireOp",EDGE,"E67")])]})]});
            fillet(context, id + "F14", {"entities" : qUnion([Q0, Q1, Q2, Q3, Q4, Q5]), "radius" : 3 * mm, "tangentPropagation" : true, "allowEdgeOverflow" : false});
        }
        {
            var Q0;
            Q0=makeQuery(id+"F1.opExtrude","CAP_EDGE",EDGE,{"disambiguationData":[OSD([sQuery(id+"F0.wireOp",EDGE,"E1.bottom")])],"isStart":false});
            fillet(context, id + "F15", {"entities" : qUnion([Q0]), "radius" : 2 * mm, "tangentPropagation" : true, "allowEdgeOverflow" : false});
        }
        {
            var Q0;
            {var subQ0=sQuery(id+"F0.wireOp",EDGE,"E21.filletArc");var subQ1=sQuery(id+"F0.wireOp",EDGE,"E7");var subQ2=sQuery(id+"F0.wireOp",EDGE,"E6");var subQ3=sQuery(id+"F0.wireOp",EDGE,"E5");var subQ4=sQuery(id+"F0.wireOp",EDGE,"E4");var subQ5=sQuery(id+"F0.wireOp",EDGE,"E22.filletArc");var subQ6=sQuery(id+"F0.wireOp",EDGE,"E1.bottom");var subQ7=sQuery(id+"F0.wireOp",EDGE,"E1.right");var subQ8=sQuery(id+"F0.wireOp",EDGE,"E1.top");var subQ9=sQuery(id+"F0.wireOp",EDGE,"E1.left");var subQ10=sQuery(id+"F0.wireOp",EDGE,"E23.filletArc");var subQ11=sQuery(id+"F0.wireOp",EDGE,"E24.filletArc");Q0=makeQuery(id+"F2.boolean.opBoolean","SPLIT",FACE,{"disambiguationData":[TD([makeQuery(id+"F1.opExtrude","SWEPT_FACE",FACE,{"disambiguationData":[OSD([subQ6])]})])],"derivedFrom":makeQuery(id+"F1.opExtrude","CAP_FACE",FACE,{"disambiguationData":[OSD([subQ6,subQ8,subQ9,subQ7,subQ4,subQ3,subQ2,subQ1,subQ0,subQ5,subQ10,subQ11])],"isStart":true})});}
            var sketch = newSketch(context, id + "F16", { "sketchPlane" : qUnion([Q0])});
            skLineSegment(sketch, "E79", {"start": v(0, 90) * mm, "end": v(0, 120) * mm, "construction": true});
            skCircle(sketch, "E80", {"center": v(0, 120) * mm, "radius": 6 * mm});
            skLineSegment(sketch, "E81", {"start": v(-15, 120) * mm, "end": v(-15, 108) * mm});
            skLineSegment(sketch, "E82", {"start": v(-15, 108) * mm, "end": v(-33, 90) * mm});
            skLineSegment(sketch, "E83", {"start": v(15, 120) * mm, "end": v(15, 108) * mm});
            skLineSegment(sketch, "E84", {"start": v(15, 108) * mm, "end": v(33, 90) * mm});
            skArc(sketch, "E85", {"start": v(15, 120) * mm, "mid": v(0, 135) * mm, "end": v(-15, 120) * mm});
            skLineSegment(sketch, "E86", {"start": v(-80, 0) * mm, "end": v(80, 0) * mm, "construction": true});
            skLineSegment(sketch, "E87.MirrorCS", {"start": v(0, -90) * mm, "end": v(0, -120) * mm, "construction": true});
            skLineSegment(sketch, "E88.MirrorCS", {"start": v(15, -120) * mm, "end": v(15, -108) * mm});
            skCircle(sketch, "E89.MirrorC", {"center": v(0, -120) * mm, "radius": 6 * mm});
            skLineSegment(sketch, "E90.MirrorCS", {"start": v(-15, -108) * mm, "end": v(-33, -90) * mm});
            skArc(sketch, "E91.MirrorCS", {"start": v(15, -120) * mm, "mid": v(0, -135) * mm, "end": v(-15, -120) * mm});
            skLineSegment(sketch, "E92.MirrorCS", {"start": v(-15, -120) * mm, "end": v(-15, -108) * mm});
            skLineSegment(sketch, "E93.MirrorCS", {"start": v(15, -108) * mm, "end": v(33, -90) * mm});
            skSolve(sketch);
        }
        {
            var Q0;
            Q0=makeQuery(id+"F16.imprint","IMPRINT",FACE,{"disambiguationData":[TD([[makeQuery(id+"F16.imprint","IMPRINT",EDGE,{"derivedFrom":sQuery(id+"F16.wireOp",EDGE,"E80")}),-1.0]])]});
            var Q1;
            Q1=makeQuery(id+"F16.imprint","IMPRINT",FACE,{"disambiguationData":[TD([[makeQuery(id+"F16.imprint","IMPRINT",EDGE,{"derivedFrom":makeQuery(id+"F1.opExtrude","CAP_EDGE",EDGE,{"disambiguationData":[OSD([sQuery(id+"F0.wireOp",EDGE,"E1.left")])],"isStart":true})}),-1.0]])]});
            var Q2;
            Q2=makeQuery(id+"F16.imprint","IMPRINT",FACE,{"disambiguationData":[TD([[makeQuery(id+"F16.imprint","IMPRINT",EDGE,{"derivedFrom":sQuery(id+"F16.wireOp",EDGE,"E91.MirrorCS")}),-1.0]])]});
            var Q3;
            Q3=makeQuery(id+"F2.opExtrude","CAP_FACE",FACE,{"disambiguationData":[OSD([sQuery(id+"F0.wireOp",EDGE,"E12"),sQuery(id+"F0.wireOp",EDGE,"E13"),sQuery(id+"F0.wireOp",EDGE,"E14"),sQuery(id+"F0.wireOp",EDGE,"E15"),sQuery(id+"F0.wireOp",EDGE,"E17.filletArc"),sQuery(id+"F0.wireOp",EDGE,"E18.filletArc"),sQuery(id+"F0.wireOp",EDGE,"E19.filletArc"),sQuery(id+"F0.wireOp",EDGE,"E20.filletArc"),sQuery(id+"F0.wireOp",EDGE,"E25.0"),sQuery(id+"F0.wireOp",EDGE,"E25.1"),sQuery(id+"F0.wireOp",EDGE,"E25.2"),sQuery(id+"F0.wireOp",EDGE,"E25.3"),sQuery(id+"F0.wireOp",EDGE,"E25.4"),sQuery(id+"F0.wireOp",EDGE,"E25.5"),sQuery(id+"F0.wireOp",EDGE,"E25.6"),sQuery(id+"F0.wireOp",EDGE,"E25.7")])],"isStart":false});
            extrude(context, id + "F17", {"entities" : qUnion([Q0, Q1, Q2]), "endBound" : BoundingType.UP_TO_SURFACE, "endBoundEntityFace" : qUnion([Q3]), "depth" : 25 * mm});
        }
    });
